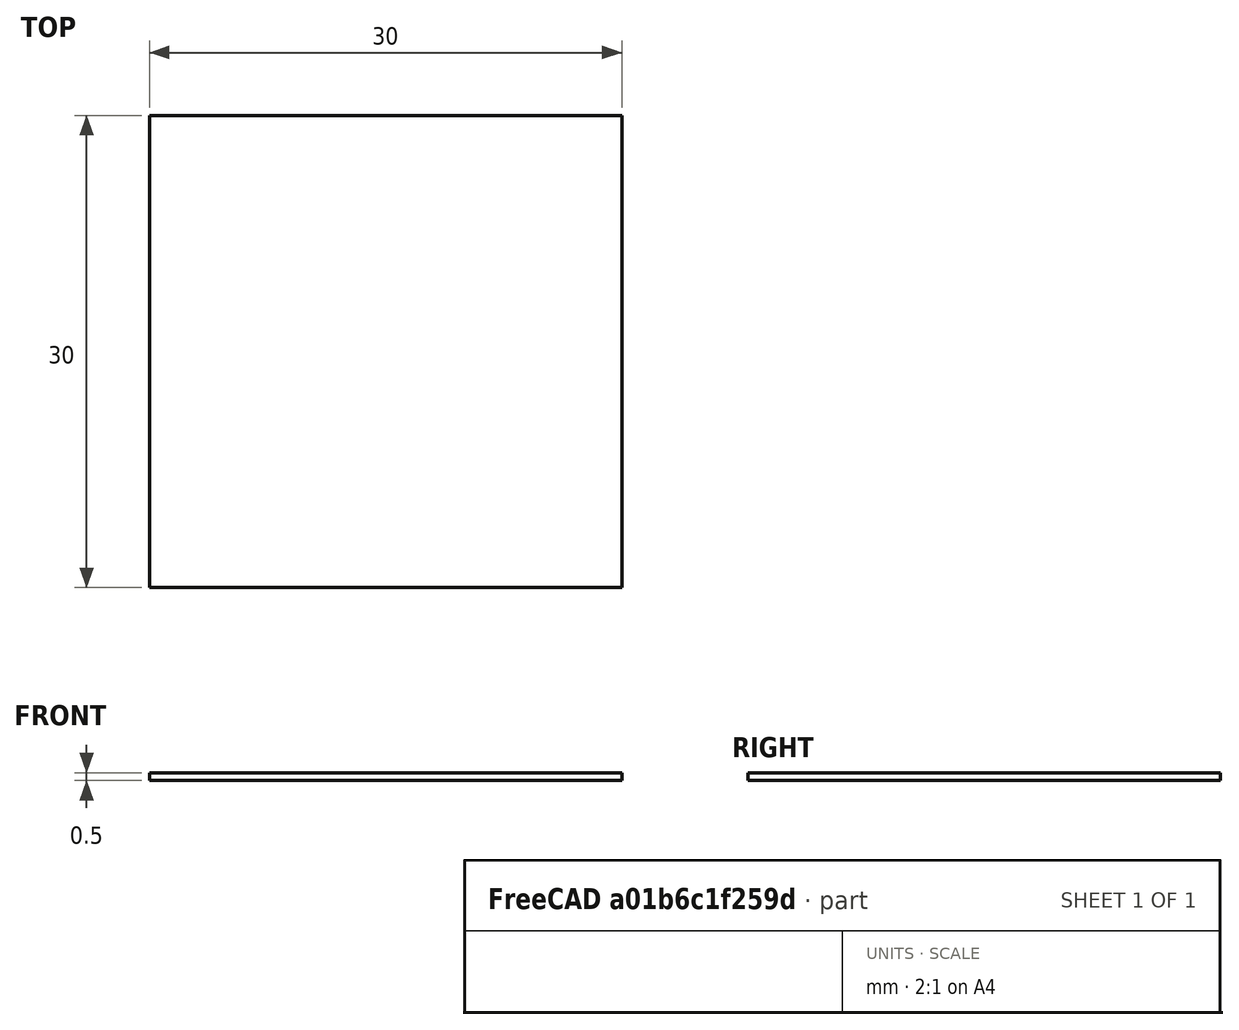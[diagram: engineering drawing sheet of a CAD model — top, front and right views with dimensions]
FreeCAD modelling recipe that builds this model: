
FCSTD DOCUMENT  (FreeCAD 0.18R14555 (Git shallow))
Label: first-layer-test
License: All rights reserved
LicenseURL: http://en.wikipedia.org/wiki/All_rights_reserved
objects: Sketcher::SketchObject×1, PartDesign::Pad×1, PartDesign::Body×1
note: 4 computed .brp shape members not serialized (recipe doc carries the construction recipe); baked Part::Feature solids carry a one-line shape summary decoded from their .brp

FEATURE [Sketcher::SketchObject] Sketch
  MapMode = 5
  Support = -> [XY_Plane]
  sketch-geometry (4):
    g0: LineSegment StartX=9e-16 StartY=0 StartZ=0 EndX=30 EndY=0 EndZ=0
    g1: LineSegment StartX=30 StartY=0 StartZ=0 EndX=30 EndY=30 EndZ=0
    g2: LineSegment StartX=30 StartY=30 StartZ=0 EndX=0 EndY=30 EndZ=0
    g3: LineSegment StartX=9e-16 StartY=30 StartZ=0 EndX=9e-16 EndY=0 EndZ=0
  constraints (11):
    c: Coincident(g0,g1)
    c: Coincident(g1,g2)
    c: Coincident(g2,g3)
    c: Coincident(g3,g0)
    c: Horizontal(g0)
    c: Horizontal(g2)
    c: Vertical(g1)
    c: Vertical(g3)
    c: Coincident(g0,g-1)
    c: Equal(g2,g1)
    c: DistanceX(g2,g2) = 30
FEATURE [PartDesign::Pad] Pad
  Length = 0.5
  Length2 = 100
  Profile = -> Sketch
  Type = 0
FEATURE [PartDesign::Body] Body
  Group = -> [Sketch,Pad]
  Origin = -> Origin
  Tip = -> Pad
